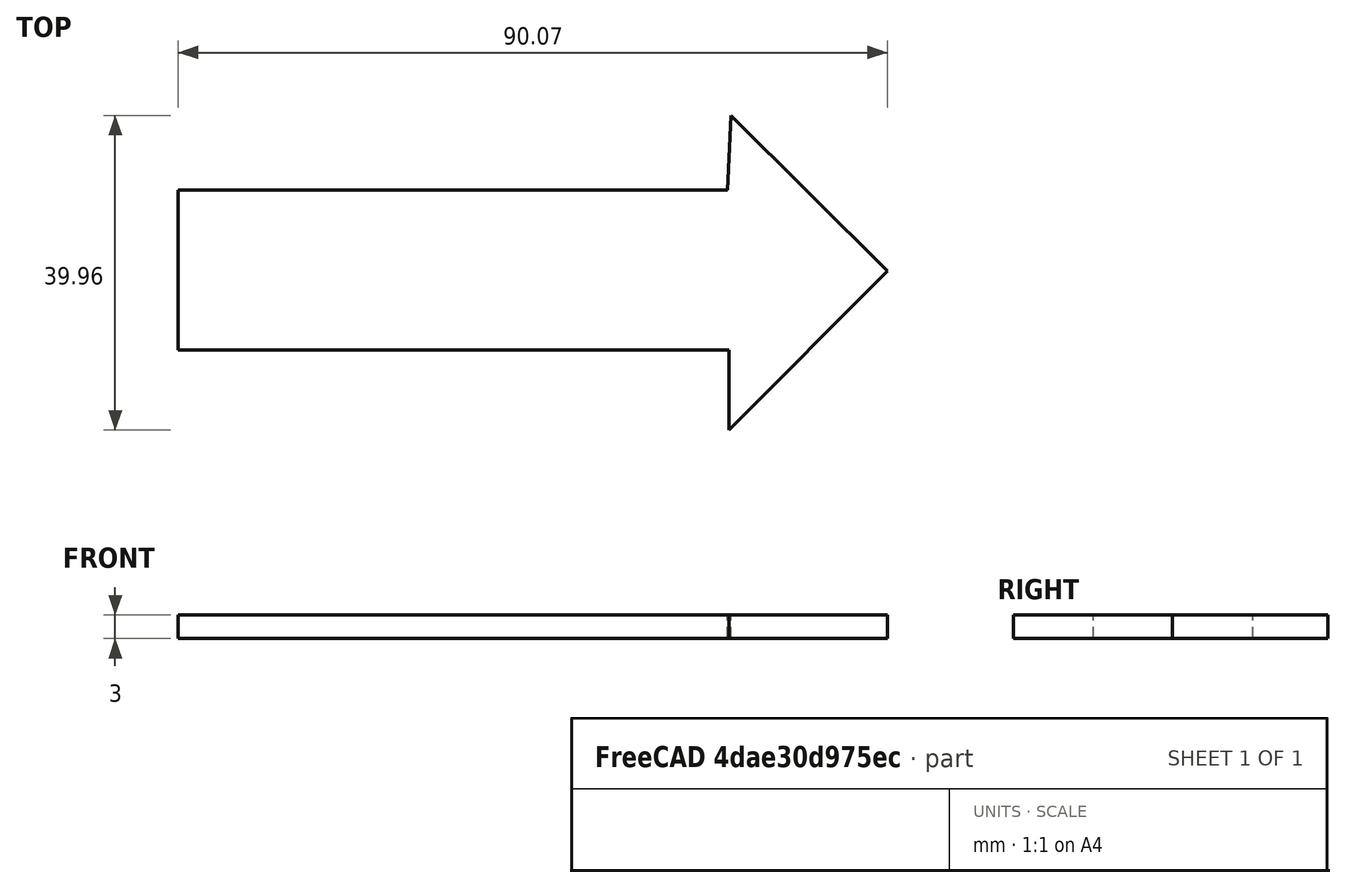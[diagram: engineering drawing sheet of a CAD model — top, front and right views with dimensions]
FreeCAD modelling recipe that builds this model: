
FCSTD DOCUMENT  (FreeCAD 1.0R39319 (Git))
Label: ojt1_t16r02_arrow
License: All rights reserved
LicenseURL: https://en.wikipedia.org/wiki/All_rights_reserved
objects: Sketcher::SketchObject×1, PartDesign::Pad×1, PartDesign::Body×1
note: 6 computed .brp shape members not serialized (recipe doc carries the construction recipe); baked Part::Feature solids carry a one-line shape summary decoded from their .brp

FEATURE [Sketcher::SketchObject] Sketch
  ArcFitTolerance = 1e-06
  AttachmentSupport = -> [XY_Plane]
  FullyConstrained = false
  MakeInternals = false
  MapMode = 5
  sketch-geometry (7):
    g0: LineSegment StartX=-30.1269 StartY=10.2538 StartZ=0 EndX=-30.1269 EndY=-10.0422 EndZ=0
    g1: LineSegment StartX=-30.1269 StartY=-10.0422 StartZ=0 EndX=39.852 EndY=-10.0422 EndZ=0
    g2: LineSegment StartX=39.852 StartY=-10.0422 StartZ=0 EndX=39.852 EndY=-20.1902 EndZ=0
    g3: LineSegment StartX=39.852 StartY=-20.1902 StartZ=0 EndX=59.9365 EndY=0 EndZ=0
    g4: LineSegment StartX=59.9365 StartY=0 StartZ=0 EndX=40.0634 EndY=19.7675 EndZ=0
    g5: LineSegment StartX=40.0634 StartY=19.7675 StartZ=0 EndX=39.6405 EndY=10.2538 EndZ=0
    g6: LineSegment StartX=39.6405 StartY=10.2538 StartZ=0 EndX=-30.1269 EndY=10.2538 EndZ=0
  constraints (12):
    c: Vertical(g0)
    c: Coincident(g0,g1)
    c: Horizontal(g1)
    c: Coincident(g1,g2)
    c: Vertical(g2)
    c: Coincident(g2,g3)
    c: PointOnObject(g3,g-1)
    c: Coincident(g3,g4)
    c: Coincident(g4,g5)
    c: Coincident(g5,g6)
    c: Coincident(g6,g0)
    c: Horizontal(g6)
FEATURE [PartDesign::Pad] Pad
  Direction = (0,0,1)
  Length = 3
  Length2 = 10
  Profile = -> Sketch
  ReferenceAxis = -> Sketch [N_Axis]
  Refine = true
  Suppressed = false
  Type = 0
FEATURE [PartDesign::Body] Body
  AllowCompound = false
  Group = -> [Sketch,Pad]
  Origin = -> Origin
  Tip = -> Pad
